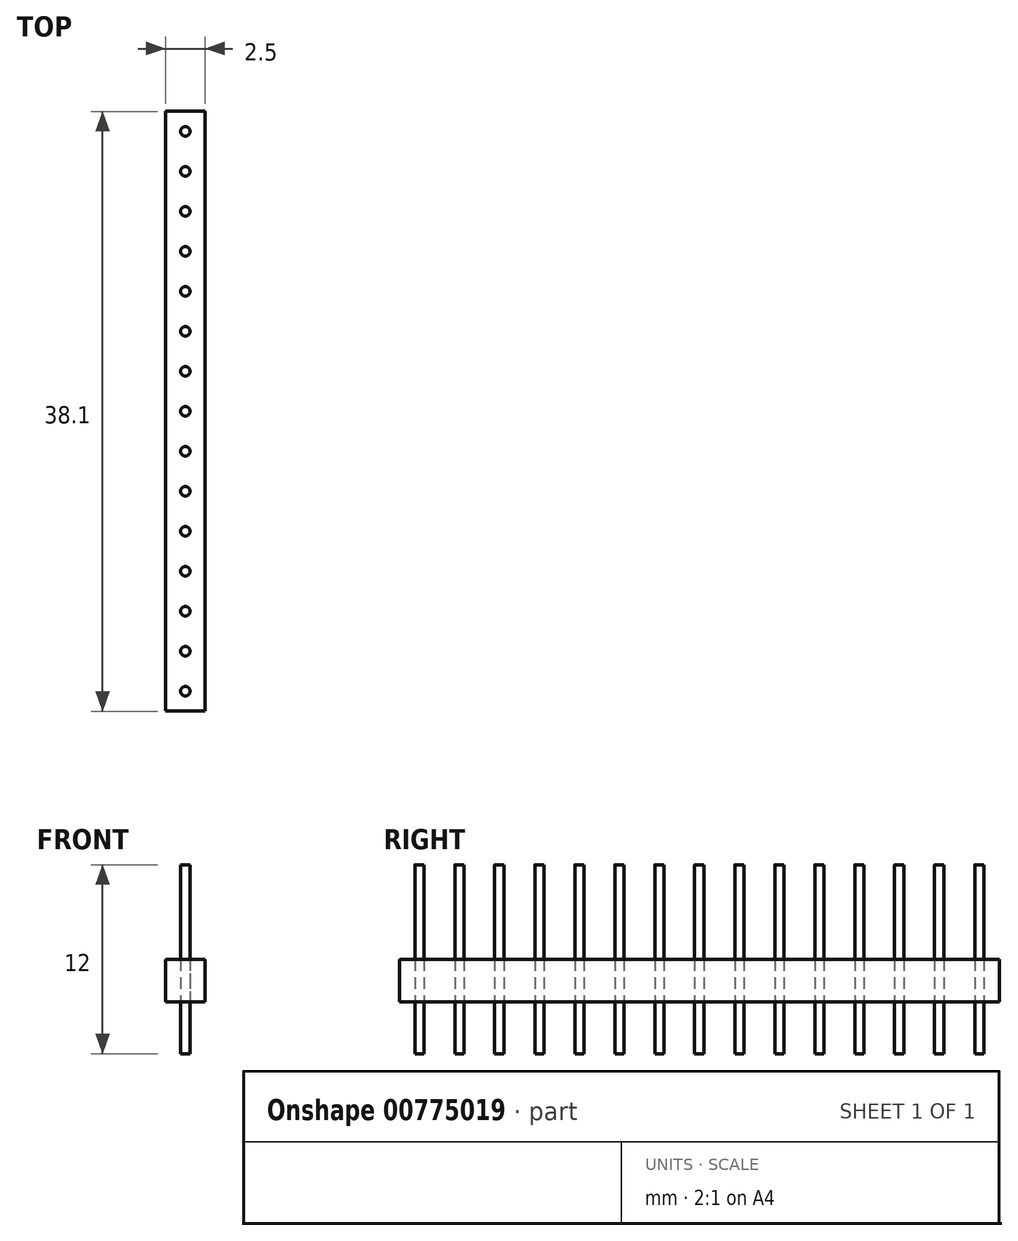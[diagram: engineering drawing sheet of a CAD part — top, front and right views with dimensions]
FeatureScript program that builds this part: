
annotation { "Feature Type Name" : "Feature", "Feature Type Description" : "" }
export const myFeature = defineFeature(function(context is Context, id is Id, definition is map)
    precondition{}
    {
        {
            var Q0;
            Q0=qCreatedBy(makeId("Top.planeOp"),FACE);
            var sketch = newSketch(context, id + "F0", { "sketchPlane" : qUnion([Q0])});
            skLineSegment(sketch, "E0.bottom", {"start": v(-1.25, 27.15) * mm, "end": v(1.25, 27.15) * mm});
            skLineSegment(sketch, "E0.top", {"start": v(-1.25, -10.95) * mm, "end": v(1.25, -10.95) * mm});
            skLineSegment(sketch, "E0.left", {"start": v(-1.25, 27.15) * mm, "end": v(-1.25, -10.95) * mm});
            skLineSegment(sketch, "E0.right", {"start": v(1.25, 27.15) * mm, "end": v(1.25, -10.95) * mm});
            skSolve(sketch);
        }
        {
            var Q0;
            Q0 = qSketchRegion(id + "F0", true);
            extrude(context, id + "F1", {"entities" : qUnion([Q0]), "depth" : 2.7 * mm, "offsetDistance" : 25 * mm});
        }
        {
            var Q0;
            Q0=makeQuery(id+"F1.opExtrude","CAP_FACE",FACE,{"disambiguationData":[OSD([sQuery(id+"F0.wireOp",EDGE,"E0.bottom"),sQuery(id+"F0.wireOp",EDGE,"E0.top"),sQuery(id+"F0.wireOp",EDGE,"E0.left"),sQuery(id+"F0.wireOp",EDGE,"E0.right")])],"isStart":false});
            var sketch = newSketch(context, id + "F2", { "sketchPlane" : qUnion([Q0])});
            skCircle(sketch, "E1", {"center": v(0, 25.88) * mm, "radius": 0.3 * mm});
            skCircle(sketch, "E2.1.0.0", {"center": v(0, 23.34) * mm, "radius": 0.3 * mm});
            skCircle(sketch, "E2.2.0.0", {"center": v(0, 20.8) * mm, "radius": 0.3 * mm});
            skCircle(sketch, "E2.3.0.0", {"center": v(0, 18.26) * mm, "radius": 0.3 * mm});
            skCircle(sketch, "E2.4.0.0", {"center": v(0, 15.72) * mm, "radius": 0.3 * mm});
            skCircle(sketch, "E2.5.0.0", {"center": v(0, 13.18) * mm, "radius": 0.3 * mm});
            skCircle(sketch, "E2.6.0.0", {"center": v(0, 10.64) * mm, "radius": 0.3 * mm});
            skCircle(sketch, "E2.7.0.0", {"center": v(0, 8.1) * mm, "radius": 0.3 * mm});
            skCircle(sketch, "E2.8.0.0", {"center": v(0, 5.56) * mm, "radius": 0.3 * mm});
            skCircle(sketch, "E2.9.0.0", {"center": v(0, 3.02) * mm, "radius": 0.3 * mm});
            skCircle(sketch, "E2.10.0.0", {"center": v(0, 0.48) * mm, "radius": 0.3 * mm});
            skCircle(sketch, "E2.11.0.0", {"center": v(0, -2.06) * mm, "radius": 0.3 * mm});
            skCircle(sketch, "E2.12.0.0", {"center": v(0, -4.6) * mm, "radius": 0.3 * mm});
            skCircle(sketch, "E2.13.0.0", {"center": v(0, -7.14) * mm, "radius": 0.3 * mm});
            skCircle(sketch, "E2.14.0.0", {"center": v(0, -9.68) * mm, "radius": 0.3 * mm});
            skLineSegment(sketch, "E2.direction1", {"start": v(0, 25.88) * mm, "end": v(0, 23.34) * mm, "construction": true});
            skSolve(sketch);
        }
        {
            var Q0;
            Q0 = qSketchRegion(id + "F2", true);
            extrude(context, id + "F3", {"entities" : qUnion([Q0]), "depth" : 6 * mm, "offsetDistance" : 25 * mm, "hasSecondDirection" : true, "secondDirectionOppositeDirection" : true, "secondDirectionDepth" : 6 * mm});
        }
    });
